# Revit family: IS_Hotline_K2748_BIM_NL
name_source: partatom
category: Plumbing Fixtures
revit_build: Autodesk Revit MEP 2016 (Build: 20161004_0715(x64)
units: mm (PartAtom-declared; Revit-internal decimal feet)

## family parameters
Always vertical = No
Cut with Voids When Loaded = No
OmniClass Number = 23.45.05.14.21
OmniClass Title = Bathtubs
Part Type = Normal
Room Calculation Point = No
Round Connector Dimension = Use Diameter
Shared = No
Work Plane-Based = No

## types (1)
- K274801 HOTLINE NEW BAD RECHTHOEKIG 180X80CM
    Accessories = www.idealstandardnederland.nl
    AreaUnits = millimeters
    Assembly Code = C1030200
    AssetType = Fixed
    BIMobject category = Bath & Spas
    BOSUseNativeGeometries = 1
    BarCode = 4015413057523
    Brand = Ideal Standard
    Brand url = http://www.idealstandard.co.uk
    Category = Bath & Spas
    CodePerformance = DIN EN 14516, DIN EN 263, DIN EN 198
    Color = Wit
    ConnectionType = Sanitair
    CurrentRevision = 1.0
    Description = Hotline new bad 1800 x 800 mm van acryl DIN EN 263. Vervaardigd volgens DIN EN 14516 en DIN EN 198. Met glasvezel verstevigd. Ingewerkte bodem- en randversteviging. Afvoergat Ø52 mm. Potenset separaat te bestellen.
    DurationUnit = jaar
    EAN code = https://4015413057523
    Edition number = 1
    ExpectedLife = 25
    Features = Bad 1800 x 800 mm van acryl DIN EN 263. Vervaardigd volgens DIN EN 14516 en DIN EN 198. Met glasvezel verstevigd. Ingewerkte bodem- en randversteviging. Afvoergat Ø52 mm. Potenset separaat te bestellen.
    Finish = Wit
    IFC Classification = Sanitary Terminal
    Installation instructions = http://www.idealstandardnederland.nl
    InstallationInstructions = http://www.idealstandardnederland.nl
    LinearUnits = millimeters
    MainColor = Wit
    Manufacturer name = Ideal Standard
    Material = Acryl
    Material main = Acrylic
    Model = K274801
    ModelNumber = K274801
    ModelReference = K274801
    NBS Reference Code = 35-06-08
    NBS Reference Description = Baths
    Name = HOTLINE NEW BAD RECHTHOEKIG 180X80CM
    NettWeight = 23 KG
    Nominal height = 465
    Nominal width = 800
    NominalHeight = 464 mm
    NominalLength = 1800 mm
    NominalWidth = 800 mm  [stored 2.62467 ft]
    OmniClass Code = 23-31 15 00
    OmniClass Description = Bathtubs
    Product Guid = 36741f60-1c6f-4077-99ca-52501292e8d6
    Product SKU = K2748
    Product data url = https://bimobject.com
    Product family = HOTLINE NEU
    Product group = Bath Tub
    Product name = HOTLINE NEU rectangular bath tub 1800x800mm
    Product url = http://www.idealstandard.de
    QR code = http://bimobject.com
    Shape = Rechthoekig
    Size = 1800x800x464 mm
    Space = Intern
    SpareParts = www.idealstandardnederland.nl
    Technical description = http://www.idealstandardnederland.nl
    URL = www.idealstandardnederland.nl
    Uniclass 1.4 Code = L7211
    Uniclass 1.4 Description = Baths
    Uniclass 2.0 Code = PR-35-06-08
    Uniclass 2.0 Description = Baths
    Uniclass 2015 Code = Pr_40_20_06_08
    Uniclass 2015 Name = Baths
    VolumeUnits = liter
    WarrantyDescription = Fabrieksgarantie
    WarrantyDurationParts = 5
    WarrantyDurationUnit = jaar
    Weight Net (Kg) = 23

note: [stored X ft] marks values corroborated as IEEE doubles in the binary element streams (Revit-internal decimal feet)

## geometry (parser evidence)
native form markers: Blend x4, Sweep x1
no freeform markers — native parametric forms only
